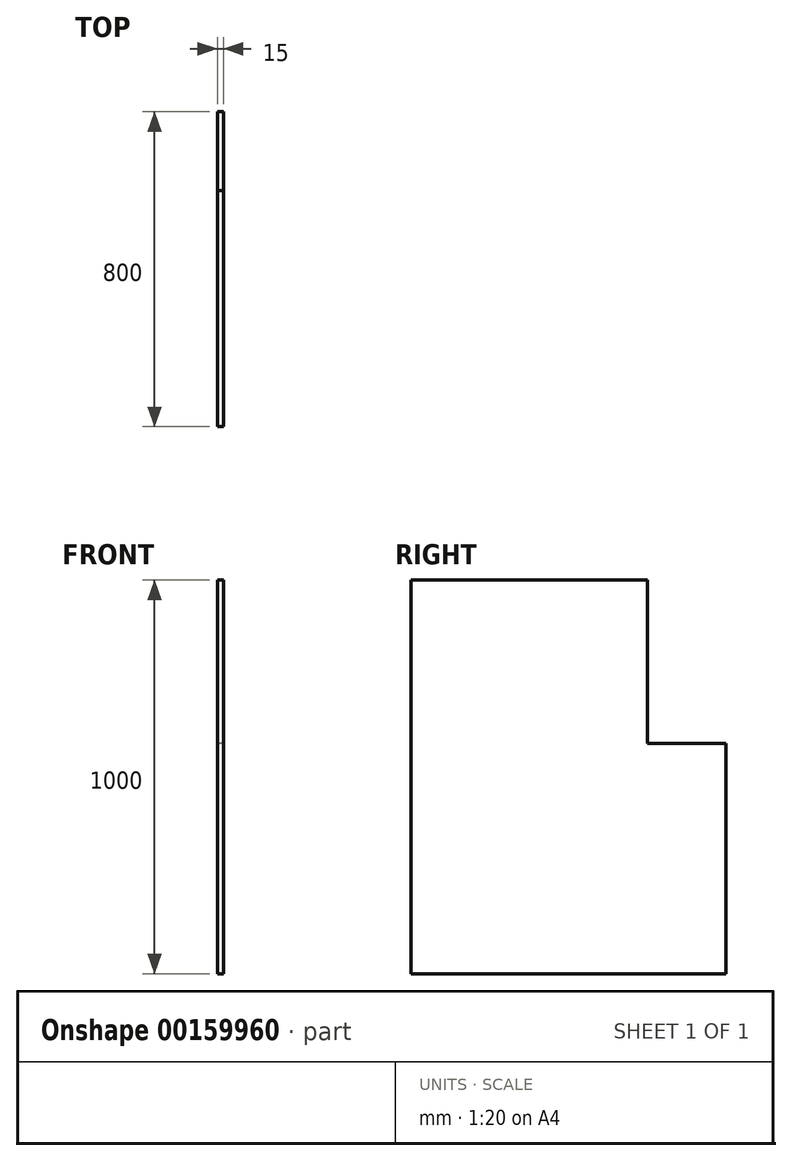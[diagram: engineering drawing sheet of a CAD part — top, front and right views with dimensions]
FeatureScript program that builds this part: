
annotation { "Feature Type Name" : "Feature", "Feature Type Description" : "" }
export const myFeature = defineFeature(function(context is Context, id is Id, definition is map)
    precondition{}
    {
        {
            var Q0;
            Q0=qCreatedBy(makeId("Right.planeOp"),FACE);
            var sketch = newSketch(context, id + "F0", { "sketchPlane" : qUnion([Q0])});
            skLineSegment(sketch, "E0.bottom", {"start": v(-501.33, 413.36) * mm, "end": v(298.67, 413.36) * mm});
            skLineSegment(sketch, "E0.top", {"start": v(-501.33, -586.64) * mm, "end": v(298.67, -586.64) * mm});
            skLineSegment(sketch, "E0.left", {"start": v(-501.33, 413.36) * mm, "end": v(-501.33, -586.64) * mm});
            skLineSegment(sketch, "E0.right", {"start": v(298.67, 413.36) * mm, "end": v(298.67, -586.64) * mm});
            skLineSegment(sketch, "E1.bottom", {"start": v(298.67, 413.36) * mm, "end": v(98.67, 413.36) * mm, "construction": true});
            skLineSegment(sketch, "E1.top", {"start": v(298.67, -1.64) * mm, "end": v(98.67, -1.64) * mm});
            skLineSegment(sketch, "E1.left", {"start": v(298.67, 413.36) * mm, "end": v(298.67, -1.64) * mm, "construction": true});
            skLineSegment(sketch, "E1.right", {"start": v(98.67, 413.36) * mm, "end": v(98.67, -1.64) * mm});
            skSolve(sketch);
        }
        {
            var Q0;
            {var subQ1=sQuery(id+"F0.wireOp",EDGE,"E0.top");Q0=makeQuery(id+"F0.imprint","IMPRINT",FACE,{"disambiguationData":[TD([[makeQuery(id+"F0.imprint","IMPRINT",EDGE,{"derivedFrom":subQ1}),1.0]])]});}
            extrude(context, id + "F1", {"entities" : qUnion([Q0]), "depth" : 15 * mm});
        }
    });
